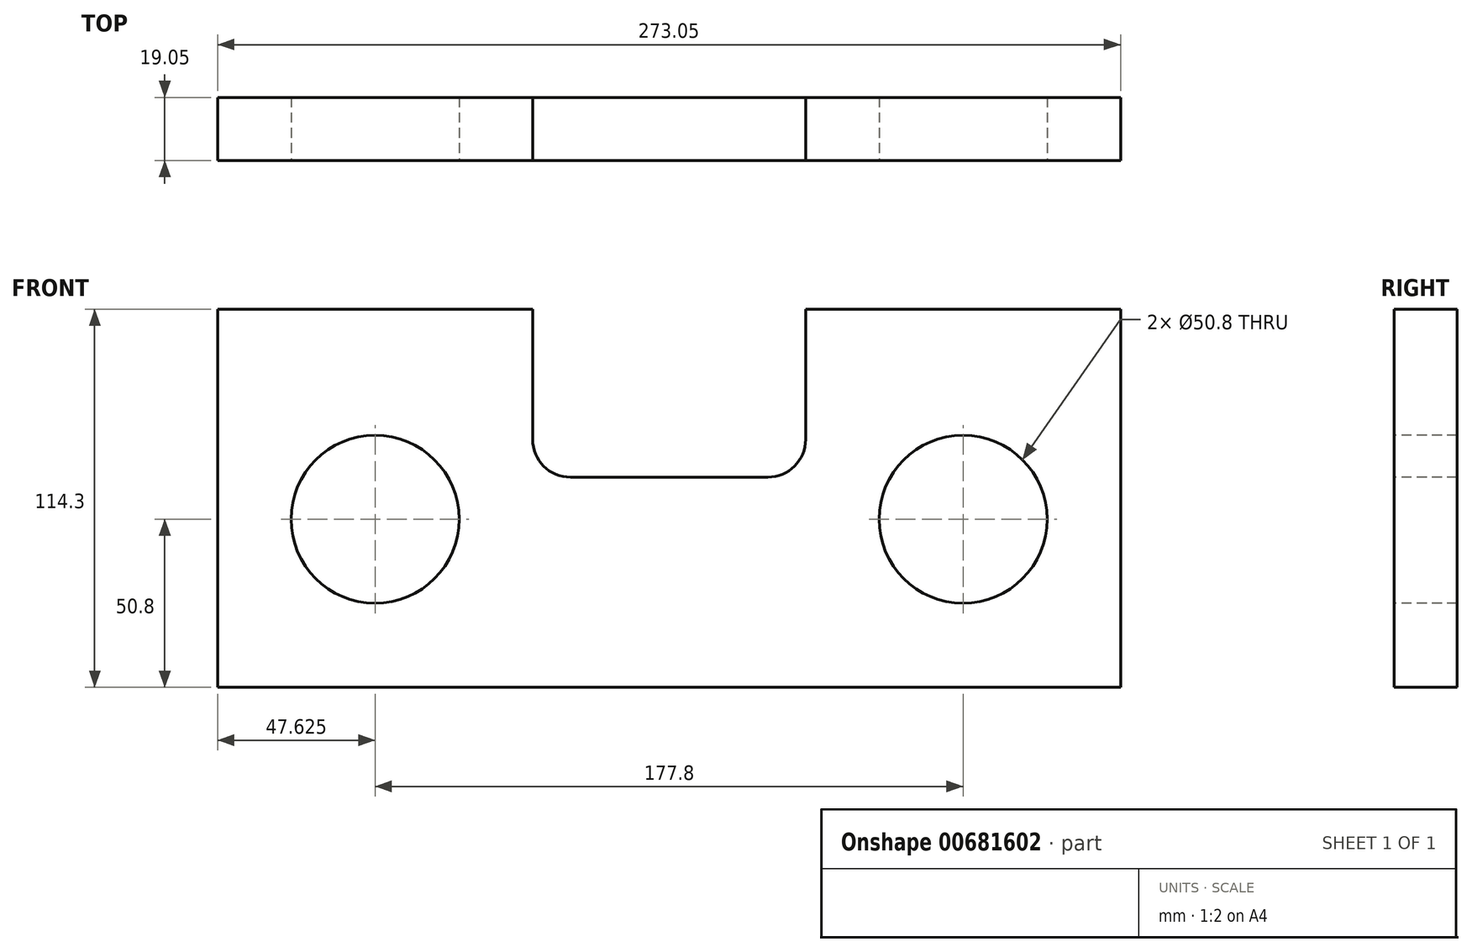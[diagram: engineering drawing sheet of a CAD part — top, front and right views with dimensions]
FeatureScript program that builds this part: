
annotation { "Feature Type Name" : "Feature", "Feature Type Description" : "" }
export const myFeature = defineFeature(function(context is Context, id is Id, definition is map)
    precondition{}
    {
        {
            var Q0;
            Q0=qCreatedBy(makeId("Front.planeOp"),FACE);
            var sketch = newSketch(context, id + "F0", { "sketchPlane" : qUnion([Q0])});
            skLineSegment(sketch, "E0.bottom", {"start": v(0, 0) * mm, "end": v(273.05, 0) * mm});
            skLineSegment(sketch, "E0.top", {"start": v(0, 114.3) * mm, "end": v(273.05, 114.3) * mm});
            skLineSegment(sketch, "E0.left", {"start": v(0, 0) * mm, "end": v(0, 114.3) * mm});
            skLineSegment(sketch, "E0.right", {"start": v(273.05, 0) * mm, "end": v(273.05, 114.3) * mm});
            skSolve(sketch);
        }
        {
            var Q0;
            Q0=qSketchRegion(id+"F0",true);
            extrude(context, id + "F1", {"entities" : qUnion([Q0]), "depth" : 19.05 * mm, "offsetDistance" : 25.4 * mm});
        }
        {
            var Q0;
            Q0=makeQuery(id+"F1.opExtrude","CAP_FACE",FACE,{"disambiguationData":[OSD([sQuery(id+"F0.wireOp",EDGE,"E0.bottom"),sQuery(id+"F0.wireOp",EDGE,"E0.top"),sQuery(id+"F0.wireOp",EDGE,"E0.left"),sQuery(id+"F0.wireOp",EDGE,"E0.right")])],"isStart":false});
            var sketch = newSketch(context, id + "F2", { "sketchPlane" : qUnion([Q0])});
            skCircle(sketch, "E1", {"center": v(47.63, 50.8) * mm, "radius": 25.4 * mm});
            skCircle(sketch, "E2", {"center": v(225.43, 50.8) * mm, "radius": 25.4 * mm});
            skSolve(sketch);
        }
        {
            var Q0;
            Q0=makeQuery(id+"F2.imprint","IMPRINT",FACE,{"disambiguationData":[TD([[makeQuery(id+"F2.imprint","IMPRINT",EDGE,{"derivedFrom":sQuery(id+"F2.wireOp",EDGE,"E2")}),1.0]])]});
            var Q1;
            Q1=makeQuery(id+"F2.imprint","IMPRINT",FACE,{"disambiguationData":[TD([[makeQuery(id+"F2.imprint","IMPRINT",EDGE,{"derivedFrom":sQuery(id+"F2.wireOp",EDGE,"E1")}),1.0]])]});
            extrude(context, id + "F3", {"entities" : qUnion([Q0, Q1]), "operationType" : NewBodyOperationType.REMOVE, "oppositeDirection" : true, "depth" : 25.4 * mm, "offsetDistance" : 25.4 * mm});
        }
        {
            var Q0;
            Q0=makeQuery(id+"F1.opExtrude","CAP_FACE",FACE,{"disambiguationData":[OSD([sQuery(id+"F0.wireOp",EDGE,"E0.bottom"),sQuery(id+"F0.wireOp",EDGE,"E0.top"),sQuery(id+"F0.wireOp",EDGE,"E0.left"),sQuery(id+"F0.wireOp",EDGE,"E0.right")])],"isStart":false});
            var sketch = newSketch(context, id + "F4", { "sketchPlane" : qUnion([Q0])});
            skLineSegment(sketch, "E3", {"start": v(95.25, 114.3) * mm, "end": v(95.25, 74.93) * mm});
            skLineSegment(sketch, "E4", {"start": v(106.68, 63.5) * mm, "end": v(166.37, 63.5) * mm});
            skLineSegment(sketch, "E5", {"start": v(177.8, 74.93) * mm, "end": v(177.8, 114.3) * mm});
            skPoint(sketch, "E6.visualSharp", {"position": v(95.25, 63.5) * mm});
            skArc(sketch, "E6.filletArc", {"start": v(95.25, 74.93) * mm, "mid": v(98.6, 66.85) * mm, "end": v(106.68, 63.5) * mm});
            skPoint(sketch, "E7.visualSharp", {"position": v(177.8, 63.5) * mm});
            skArc(sketch, "E7.filletArc", {"start": v(166.37, 63.5) * mm, "mid": v(174.45, 66.85) * mm, "end": v(177.8, 74.93) * mm});
            skSolve(sketch);
        }
        {
            var Q0;
            Q0=qSketchRegion(id+"F4",true);
            var Q1;
            {var subQ1=sQuery(id+"F4.wireOp",EDGE,"E3");Q1=makeQuery(id+"F4.imprint","IMPRINT",FACE,{"disambiguationData":[TD([[makeQuery(id+"F4.imprint","IMPRINT",EDGE,{"derivedFrom":subQ1}),1.0]])]});}
            extrude(context, id + "F5", {"entities" : qUnion([Q0, Q1]), "operationType" : NewBodyOperationType.REMOVE, "oppositeDirection" : true, "depth" : 25.4 * mm, "offsetDistance" : 25.4 * mm});
        }
    });
